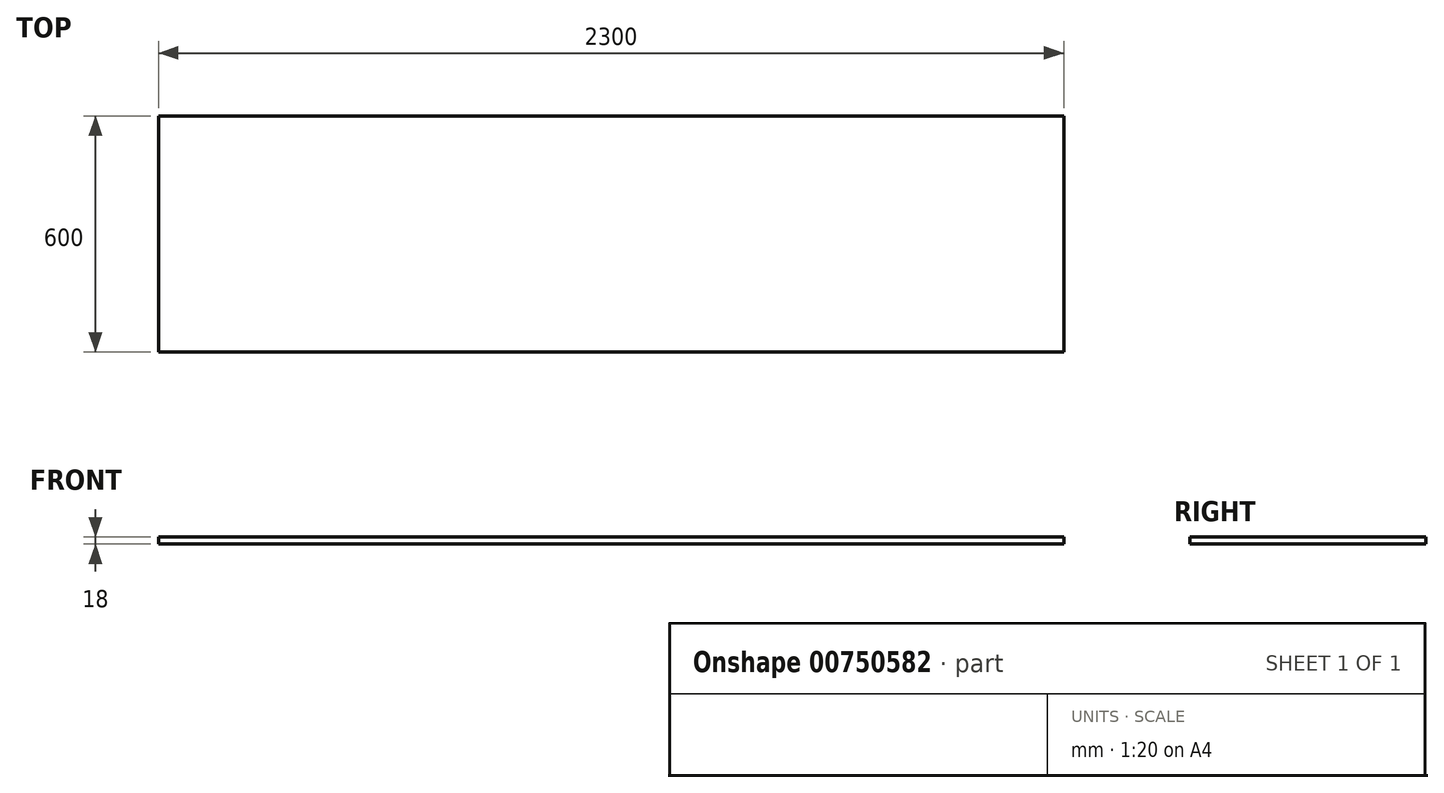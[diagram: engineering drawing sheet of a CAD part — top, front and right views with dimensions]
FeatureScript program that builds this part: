
annotation { "Feature Type Name" : "Feature", "Feature Type Description" : "" }
export const myFeature = defineFeature(function(context is Context, id is Id, definition is map)
    precondition{}
    {
        {
            var Q0;
            Q0=qCreatedBy(makeId("Top.planeOp"),FACE);
            var sketch = newSketch(context, id + "F0", { "sketchPlane" : qUnion([Q0])});
            skLineSegment(sketch, "E0.bottom", {"start": v(1150, -300) * mm, "end": v(-1150, -300) * mm});
            skLineSegment(sketch, "E0.top", {"start": v(1150, 300) * mm, "end": v(-1150, 300) * mm});
            skLineSegment(sketch, "E0.left", {"start": v(1150, -300) * mm, "end": v(1150, 300) * mm});
            skLineSegment(sketch, "E0.right", {"start": v(-1150, -300) * mm, "end": v(-1150, 300) * mm});
            skPoint(sketch, "E0.middle", {"position": v(0, 0) * mm});
            skSolve(sketch);
        }
        {
            var Q0;
            Q0 = qSketchRegion(id + "F0", true);
            extrude(context, id + "F1", {"entities" : qUnion([Q0]), "depth" : 18 * mm, "offsetDistance" : 25 * mm});
        }
    });
